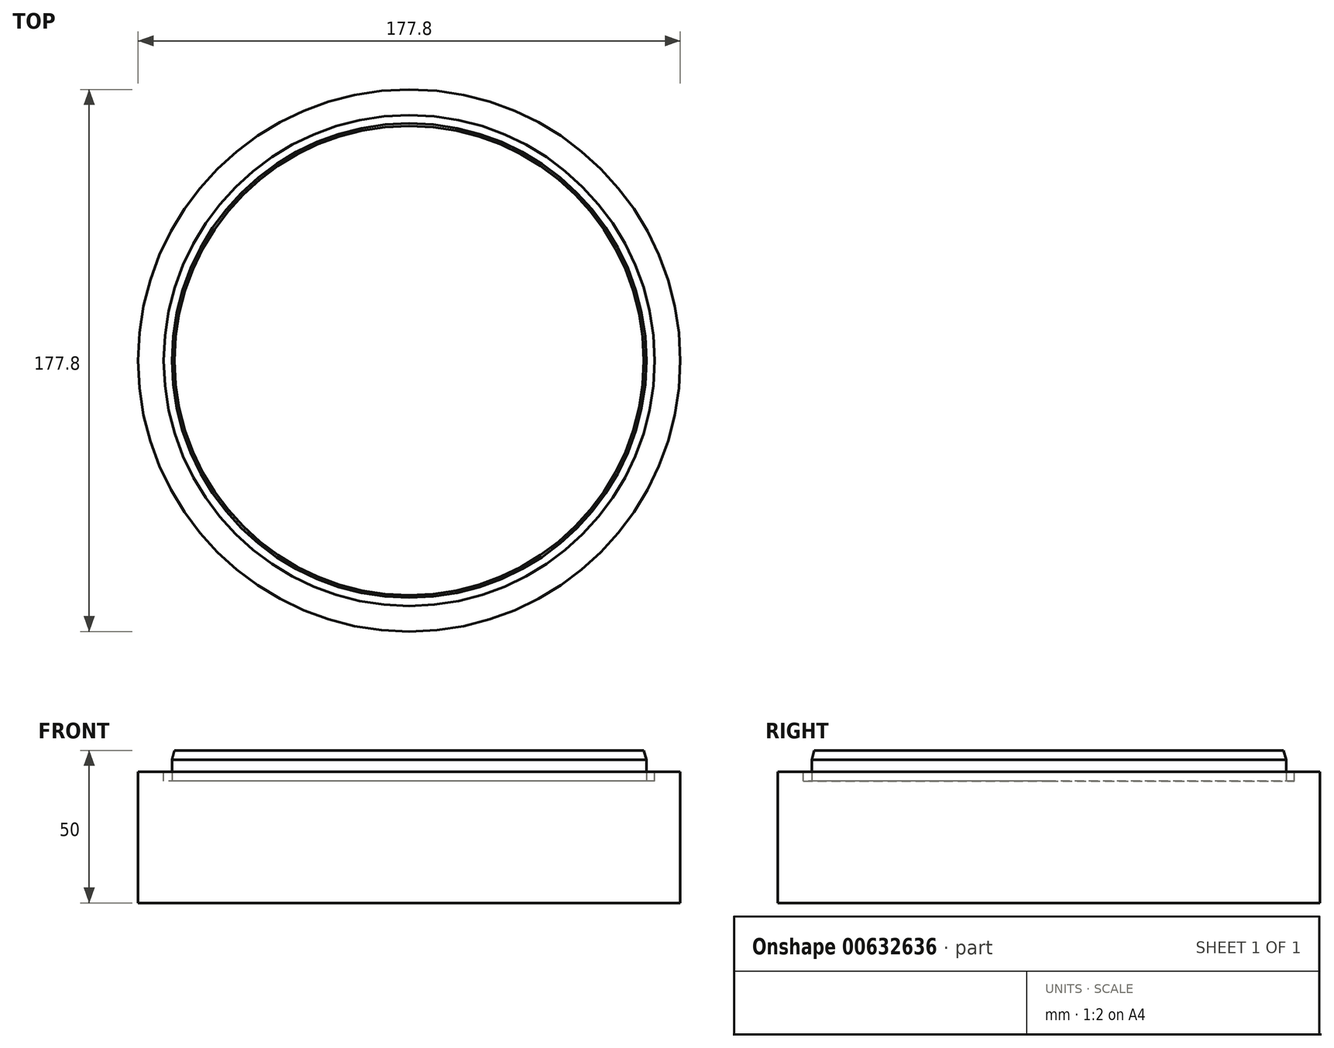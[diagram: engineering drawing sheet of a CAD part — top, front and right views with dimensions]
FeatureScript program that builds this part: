
annotation { "Feature Type Name" : "Feature", "Feature Type Description" : "" }
export const myFeature = defineFeature(function(context is Context, id is Id, definition is map)
    precondition{}
    {
        {
            var Q0;
            Q0=qCreatedBy(makeId("Front.planeOp"),FACE);
            var sketch = newSketch(context, id + "F0", { "sketchPlane" : qUnion([Q0])});
            skLineSegment(sketch, "E0", {"start": v(0, 0) * mm, "end": v(77.78, 0) * mm});
            skLineSegment(sketch, "E1", {"start": v(77.78, 0) * mm, "end": v(77.78, -7) * mm});
            skLineSegment(sketch, "E2", {"start": v(77.78, -7) * mm, "end": v(88.9, -7) * mm});
            skLineSegment(sketch, "E3", {"start": v(88.9, -7) * mm, "end": v(88.9, -50) * mm});
            skLineSegment(sketch, "E4", {"start": v(88.9, -50) * mm, "end": v(0, -50) * mm});
            skLineSegment(sketch, "E5", {"start": v(0, -50) * mm, "end": v(0, 0) * mm});
            skSolve(sketch);
        }
        {
            var Q0;
            Q0=makeQuery(id+"F0.imprint","IMPRINT",FACE,{"disambiguationData":[TD([[makeQuery(id+"F0.imprint","IMPRINT",EDGE,{"derivedFrom":sQuery(id+"F0.wireOp",EDGE,"E0")}),-1.0]])]});
            var Q1;
            Q1=sQuery(id+"F0.wireOp",EDGE,"E5");
            revolve(context, id + "F1", {"entities" : qUnion([Q0]), "axis" : qUnion([Q1]), "revolveType" : RevolveType.FULL});
        }
        {
            var Q0;
            Q0=makeQuery(id+"F1.opRevolve","SWEPT_EDGE",EDGE,{"disambiguationData":[OSD([sQuery(id+"F0.wireOp",EDGE,"E0"),sQuery(id+"F0.wireOp",EDGE,"E1")])]});
            chamfer(context, id + "F2", {"entities" : qUnion([Q0]), "chamferType" : ChamferType.OFFSET_ANGLE, "width" : 3 * mm, "oppositeDirection" : false, "angle" : 15 * degree, "tangentPropagation" : true});
        }
        {
            var Q0;
            Q0=qCreatedBy(makeId("Front.planeOp"),FACE);
            var sketch = newSketch(context, id + "F3", { "sketchPlane" : qUnion([Q0])});
            skLineSegment(sketch, "E6", {"start": v(80.5, -7) * mm, "end": v(80.5, -10) * mm});
            skLineSegment(sketch, "E7", {"start": v(80.5, -10) * mm, "end": v(77.78, -10) * mm});
            skLineSegment(sketch, "E8", {"start": v(80.5, -7) * mm, "end": v(77.78, -7) * mm});
            skLineSegment(sketch, "E9", {"start": v(77.78, -10) * mm, "end": v(77.78, -7) * mm});
            skLineSegment(sketch, "E10", {"start": v(0, -56.5) * mm, "end": v(0, 39.57) * mm, "construction": true});
            skSolve(sketch);
        }
        {
            var Q0;
            Q0 = qSketchRegion(id + "F3", true);
            var Q1;
            Q1=sQuery(id+"F3.wireOp",EDGE,"E10");
            revolve(context, id + "F4", {"operationType" : NewBodyOperationType.REMOVE, "entities" : qUnion([Q0]), "axis" : qUnion([Q1]), "revolveType" : RevolveType.FULL, "oppositeDirection" : true});
        }
    });
